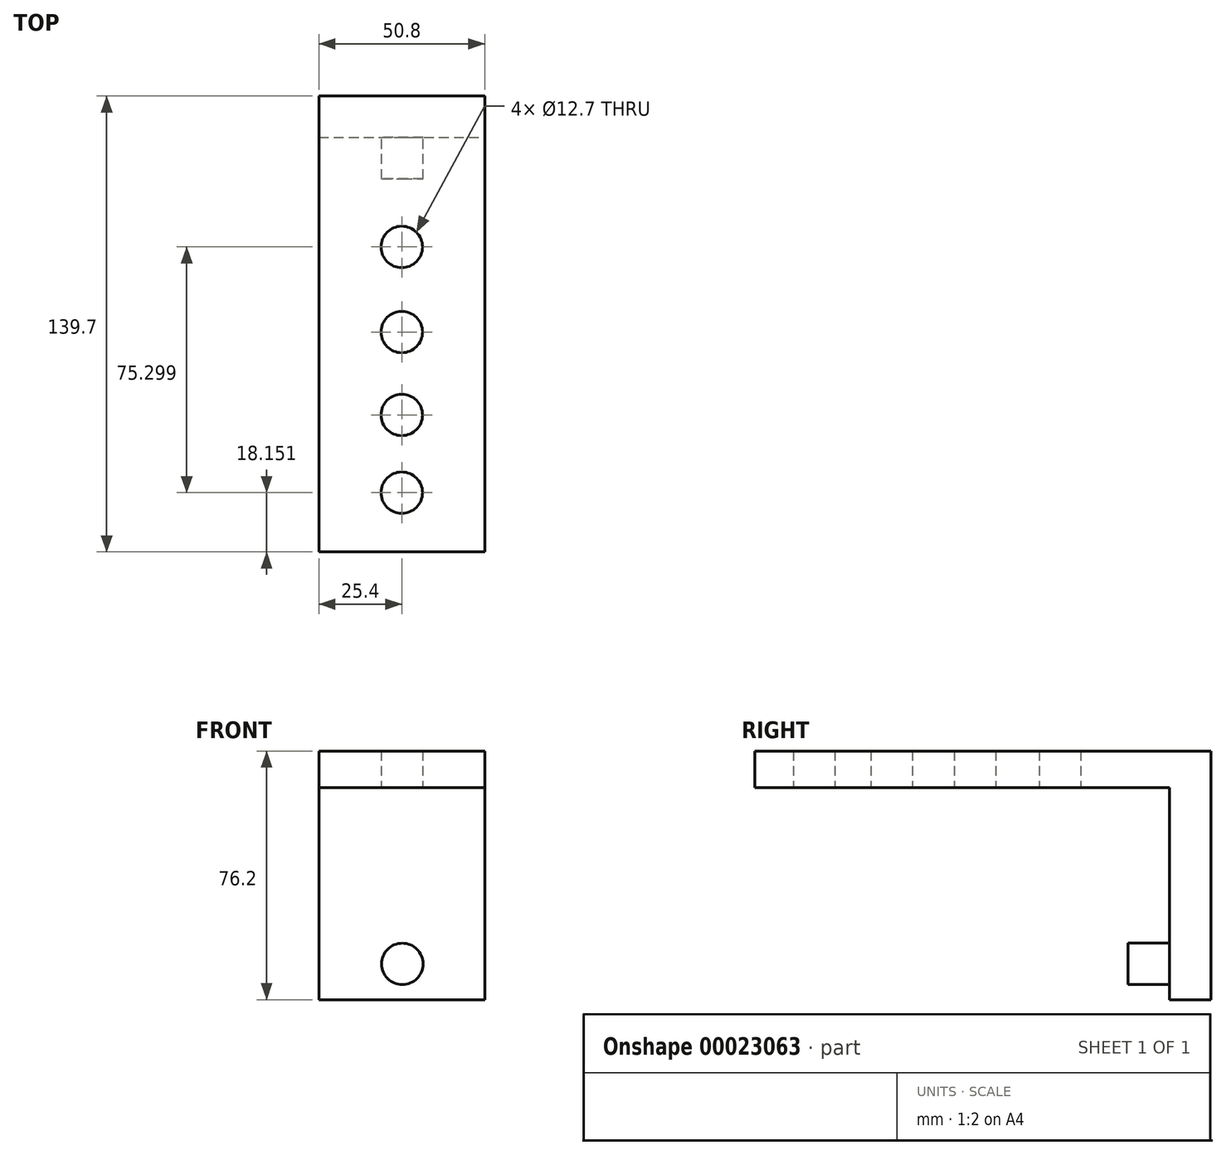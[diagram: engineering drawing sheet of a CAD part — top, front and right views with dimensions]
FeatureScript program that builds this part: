
annotation { "Feature Type Name" : "Feature", "Feature Type Description" : "" }
export const myFeature = defineFeature(function(context is Context, id is Id, definition is map)
    precondition{}
    {
        {
            var Q0;
            Q0=qCreatedBy(makeId("Front.planeOp"),FACE);
            var sketch = newSketch(context, id + "F0", { "sketchPlane" : qUnion([Q0])});
            skLineSegment(sketch, "E0.bottom", {"start": v(0, 0) * mm, "end": v(50.8, 0) * mm});
            skLineSegment(sketch, "E0.top", {"start": v(0, 76.2) * mm, "end": v(50.8, 76.2) * mm});
            skLineSegment(sketch, "E0.left", {"start": v(0, 0) * mm, "end": v(0, 76.2) * mm});
            skLineSegment(sketch, "E0.right", {"start": v(50.8, 0) * mm, "end": v(50.8, 76.2) * mm});
            skPoint(sketch, "E1", {"position": v(25.96, 10.98) * mm});
            skCircle(sketch, "E2", {"center": v(25.96, 10.98) * mm, "radius": 6.35 * mm});
            skLineSegment(sketch, "E3", {"start": v(50.8, 64.96) * mm, "end": v(0, 64.96) * mm});
            skSolve(sketch);
        }
        {
            var Q0;
            Q0=makeQuery(id+"F0.imprint","IMPRINT",FACE,{"disambiguationData":[TD([[makeQuery(id+"F0.imprint","IMPRINT",EDGE,{"derivedFrom":sQuery(id+"F0.wireOp",EDGE,"E0.bottom")}),1.0]])]});
            var Q1;
            Q1=makeQuery(id+"F0.imprint","IMPRINT",FACE,{"disambiguationData":[TD([[makeQuery(id+"F0.imprint","IMPRINT",EDGE,{"derivedFrom":sQuery(id+"F0.wireOp",EDGE,"E2")}),1.0]])]});
            extrude(context, id + "F1", {"entities" : qUnion([Q0, Q1]), "depth" : 12.7 * mm});
        }
        {
            var Q0;
            Q0=makeQuery(id+"F1.opExtrude","CAP_FACE",FACE,{"disambiguationData":[OSD([sQuery(id+"F0.wireOp",EDGE,"E0.bottom"),sQuery(id+"F0.wireOp",EDGE,"E0.top"),sQuery(id+"F0.wireOp",EDGE,"E0.left"),sQuery(id+"F0.wireOp",EDGE,"E0.right")])],"isStart":false});
            var sketch = newSketch(context, id + "F2", { "sketchPlane" : qUnion([Q0])});
            skCircle(sketch, "E4", {"center": v(25.58, 10.95) * mm, "radius": 6.35 * mm});
            skSolve(sketch);
        }
        {
            var Q0;
            Q0=makeQuery(id+"F2.imprint","IMPRINT",FACE,{"disambiguationData":[TD([[makeQuery(id+"F2.imprint","IMPRINT",EDGE,{"derivedFrom":sQuery(id+"F2.wireOp",EDGE,"E4")}),1.0]])]});
            extrude(context, id + "F3", {"entities" : qUnion([Q0]), "operationType" : NewBodyOperationType.ADD, "depth" : 12.7 * mm});
        }
        {
            var Q0;
            {var subQ2=sQuery(id+"F0.wireOp",EDGE,"E0.top");Q0=makeQuery(id+"F0.imprint","IMPRINT",FACE,{"disambiguationData":[TD([[makeQuery(id+"F0.imprint","IMPRINT",EDGE,{"derivedFrom":subQ2}),-1.0]])]});}
            extrude(context, id + "F4", {"entities" : qUnion([Q0]), "operationType" : NewBodyOperationType.ADD, "depth" : 139.7 * mm});
        }
        {
            var Q0;
            Q0=makeQuery(id+"F4.opExtrude","SWEPT_FACE",FACE,{"disambiguationData":[OSD([sQuery(id+"F0.wireOp",EDGE,"E3")])]});
            var sketch = newSketch(context, id + "F5", { "sketchPlane" : qUnion([Q0])});
            skLineSegment(sketch, "E5", {"start": v(25.4, 139.7) * mm, "end": v(25.4, 12.7) * mm});
            skPoint(sketch, "E6", {"position": v(25.4, 121.55) * mm});
            skPoint(sketch, "E7", {"position": v(25.4, 97.72) * mm});
            skPoint(sketch, "E8", {"position": v(25.4, 72.3) * mm});
            skPoint(sketch, "E9", {"position": v(25.4, 46.25) * mm});
            skCircle(sketch, "E10", {"center": v(25.4, 121.55) * mm, "radius": 6.35 * mm});
            skCircle(sketch, "E11", {"center": v(25.4, 97.72) * mm, "radius": 6.35 * mm});
            skCircle(sketch, "E12", {"center": v(25.4, 72.3) * mm, "radius": 6.35 * mm});
            skCircle(sketch, "E13", {"center": v(25.4, 46.25) * mm, "radius": 6.35 * mm});
            skSolve(sketch);
        }
        {
            var Q0;
            Q0=sQuery(id+"F5.wireOp",VERTEX,"E9");
            var Q1;
            Q1=sQuery(id+"F5.wireOp",VERTEX,"E8");
            var Q2;
            Q2=sQuery(id+"F5.wireOp",VERTEX,"E7");
            var Q3;
            Q3=sQuery(id+"F5.wireOp",VERTEX,"E6");
            var Q4;
            Q4=makeQuery(id+"F1.opExtrude","SWEPT_BODY",BODY,{"disambiguationData":[OSD([sQuery(id+"F0.wireOp",EDGE,"E0.bottom"),sQuery(id+"F0.wireOp",EDGE,"E0.left"),sQuery(id+"F0.wireOp",EDGE,"E0.right"),sQuery(id+"F0.wireOp",EDGE,"E3")])]});
            hole(context, id + "F6", {"style" : HoleStyle.SIMPLE, "holeDiameter" : 12.7 * mm, "endStyle" : HoleEndStyle.THROUGH, "locations" : qUnion([Q0, Q1, Q2, Q3]), "scope" : qUnion([Q4])});
        }
    });
